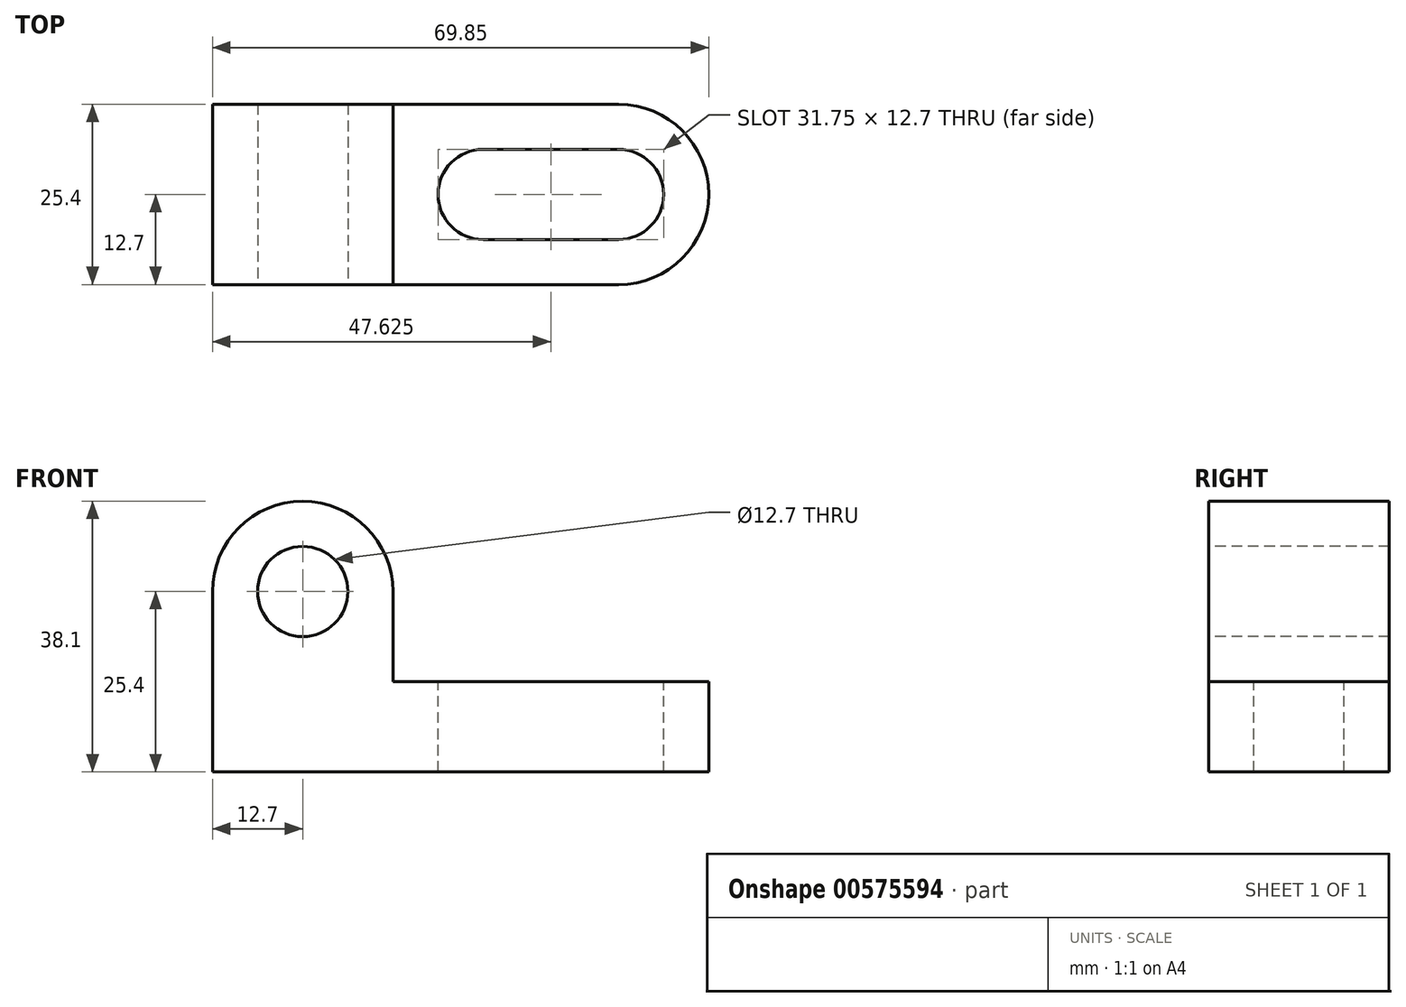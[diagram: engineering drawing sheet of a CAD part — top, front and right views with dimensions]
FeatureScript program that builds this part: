
annotation { "Feature Type Name" : "Feature", "Feature Type Description" : "" }
export const myFeature = defineFeature(function(context is Context, id is Id, definition is map)
    precondition{}
    {
        {
            var Q0;
            Q0=qCreatedBy(makeId("Front.planeOp"),FACE);
            var sketch = newSketch(context, id + "F0", { "sketchPlane" : qUnion([Q0])});
            skLineSegment(sketch, "E0", {"start": v(0, 0) * mm, "end": v(44.45, 0) * mm});
            skLineSegment(sketch, "E1", {"start": v(44.45, 0) * mm, "end": v(44.45, 12.7) * mm});
            skLineSegment(sketch, "E2", {"start": v(44.45, 12.7) * mm, "end": v(0, 12.7) * mm});
            skLineSegment(sketch, "E3", {"start": v(0, 12.7) * mm, "end": v(0, 0) * mm});
            skSolve(sketch);
        }
        {
            var Q0;
            Q0 = qSketchRegion(id + "F0", true);
            extrude(context, id + "F1", {"entities" : qUnion([Q0]), "depth" : 25.4 * mm, "offsetDistance" : 25.4 * mm});
        }
        {
            var Q0;
            Q0=qCreatedBy(makeId("Top.planeOp"),FACE);
            var sketch = newSketch(context, id + "F2", { "sketchPlane" : qUnion([Q0])});
            skLineSegment(sketch, "E4", {"start": v(0, 0) * mm, "end": v(-25.4, 0) * mm});
            skLineSegment(sketch, "E5", {"start": v(-25.4, 0) * mm, "end": v(-25.4, -25.4) * mm});
            skLineSegment(sketch, "E6", {"start": v(-25.4, -25.4) * mm, "end": v(0, -25.4) * mm});
            skLineSegment(sketch, "E7", {"start": v(0, 0) * mm, "end": v(0, -25.4) * mm});
            skSolve(sketch);
        }
        {
            var Q0;
            Q0 = qSketchRegion(id + "F2", true);
            extrude(context, id + "F3", {"entities" : qUnion([Q0]), "operationType" : NewBodyOperationType.ADD, "depth" : 25.4 * mm, "offsetDistance" : 25.4 * mm});
        }
        {
            var Q0;
            Q0=makeQuery(id+"F3.boolean.opBoolean","MERGE",FACE,{"derivedFrom":[makeQuery(id+"F1.opExtrude","CAP_FACE",FACE,{"disambiguationData":[OSD([sQuery(id+"F0.wireOp",EDGE,"E0"),sQuery(id+"F0.wireOp",EDGE,"E1"),sQuery(id+"F0.wireOp",EDGE,"E2"),sQuery(id+"F0.wireOp",EDGE,"E3")])],"isStart":false}),makeQuery(id+"F3.opExtrude","SWEPT_FACE",FACE,{"disambiguationData":[OSD([sQuery(id+"F2.wireOp",EDGE,"E6")])]})]});
            var sketch = newSketch(context, id + "F4", { "sketchPlane" : qUnion([Q0])});
            skCircle(sketch, "E8", {"center": v(-12.7, 25.4) * mm, "radius": 12.7 * mm});
            skCircle(sketch, "E9", {"center": v(-12.7, 25.4) * mm, "radius": 6.35 * mm});
            skSolve(sketch);
        }
        {
            var Q0;
            {var subQ0=sQuery(id+"F4.wireOp",EDGE,"E9");var subQ1=makeQuery(id+"F3.opExtrude","CAP_EDGE",EDGE,{"disambiguationData":[OSD([sQuery(id+"F2.wireOp",EDGE,"E6")])],"isStart":false});var subQ2=makeQuery(id+"F4.imprint","INTERSECT",VERTEX,{"disambiguationData":[OD(0.0)],"derivedFrom":[subQ1,subQ0]});Q0=makeQuery(id+"F4.imprint","IMPRINT",FACE,{"disambiguationData":[TD([[makeQuery(id+"F4.imprint","IMPRINT",EDGE,{"disambiguationData":[TD([[subQ2,-1.0]])],"derivedFrom":subQ0}),1.0]])]});}
            extrude(context, id + "F5", {"entities" : qUnion([Q0]), "operationType" : NewBodyOperationType.REMOVE, "oppositeDirection" : true, "depth" : 25.4 * mm, "offsetDistance" : 25.4 * mm});
        }
        {
            var Q0;
            Q0 = qSketchRegion(id + "F4", true);
            extrude(context, id + "F6", {"entities" : qUnion([Q0]), "operationType" : NewBodyOperationType.ADD, "oppositeDirection" : true, "depth" : 25.4 * mm, "offsetDistance" : 25.4 * mm});
        }
        {
            var Q0;
            Q0=makeQuery(id+"F4p5D8ICvT5H6dq_1.boolean.opBoolean","MERGE",FACE,{"derivedFrom":[makeQuery(id+"F1.opExtrude","SWEPT_FACE",FACE,{"disambiguationData":[OSD([sQuery(id+"F0.wireOp",EDGE,"E2")])]}),makeQuery(id+"F4p5D8ICvT5H6dq_1.opExtrude","CAP_FACE",FACE,{"disambiguationData":[OSD([sQuery(id+"FcTYjywcUDVyugP_1.wireOp",EDGE,"iPGJ9tcP-EmtL-AYoD-1q8c-tBGEklNZxg7i"),sQuery(id+"FcTYjywcUDVyugP_1.wireOp",EDGE,"7xFsJBxQ-oIYL-tNjA-ragY-xBY74L1l6deu")])],"isStart":false})]});
            var sketch = newSketch(context, id + "F7", { "sketchPlane" : qUnion([Q0])});
            skLineSegment(sketch, "E10", {"start": v(0, 0) * mm, "end": v(0, -12.7) * mm});
            skLineSegment(sketch, "E11", {"start": v(0, -12.7) * mm, "end": v(12.7, -12.7) * mm});
            skCircle(sketch, "E12", {"center": v(12.7, -12.7) * mm, "radius": 6.35 * mm});
            skLineSegment(sketch, "E13", {"start": v(12.7, -12.7) * mm, "end": v(31.75, -12.7) * mm});
            skCircle(sketch, "E14", {"center": v(31.75, -12.7) * mm, "radius": 6.35 * mm});
            skLineSegment(sketch, "E15", {"start": v(31.75, -12.7) * mm, "end": v(31.75, -6.35) * mm});
            skLineSegment(sketch, "E16", {"start": v(31.75, -6.35) * mm, "end": v(12.7, -6.35) * mm});
            skLineSegment(sketch, "E17", {"start": v(12.7, -6.35) * mm, "end": v(12.7, -19.05) * mm});
            skLineSegment(sketch, "E18", {"start": v(12.7, -19.05) * mm, "end": v(31.75, -19.05) * mm});
            skSolve(sketch);
        }
        {
            var Q0;
            Q0 = qSketchRegion(id + "F7", true);
            extrude(context, id + "F8", {"entities" : qUnion([Q0]), "operationType" : NewBodyOperationType.REMOVE, "oppositeDirection" : true, "depth" : 25.4 * mm, "offsetDistance" : 25.4 * mm});
        }
        {
            var Q0;
            Q0=makeQuery(id+"F1.opExtrude","CAP_EDGE",EDGE,{"disambiguationData":[OSD([sQuery(id+"F0.wireOp",EDGE,"E1")])],"isStart":false});
            fillet(context, id + "F9", {"entities" : qUnion([Q0]), "radius" : 12.7 * mm, "tangentPropagation" : true, "allowEdgeOverflow" : false});
        }
        {
            var Q0;
            Q0=makeQuery(id+"F1.opExtrude","CAP_EDGE",EDGE,{"disambiguationData":[OSD([sQuery(id+"F0.wireOp",EDGE,"E1")])],"isStart":true});
            fillet(context, id + "F10", {"entities" : qUnion([Q0]), "radius" : 12.7 * mm, "tangentPropagation" : true, "allowEdgeOverflow" : false});
        }
    });
